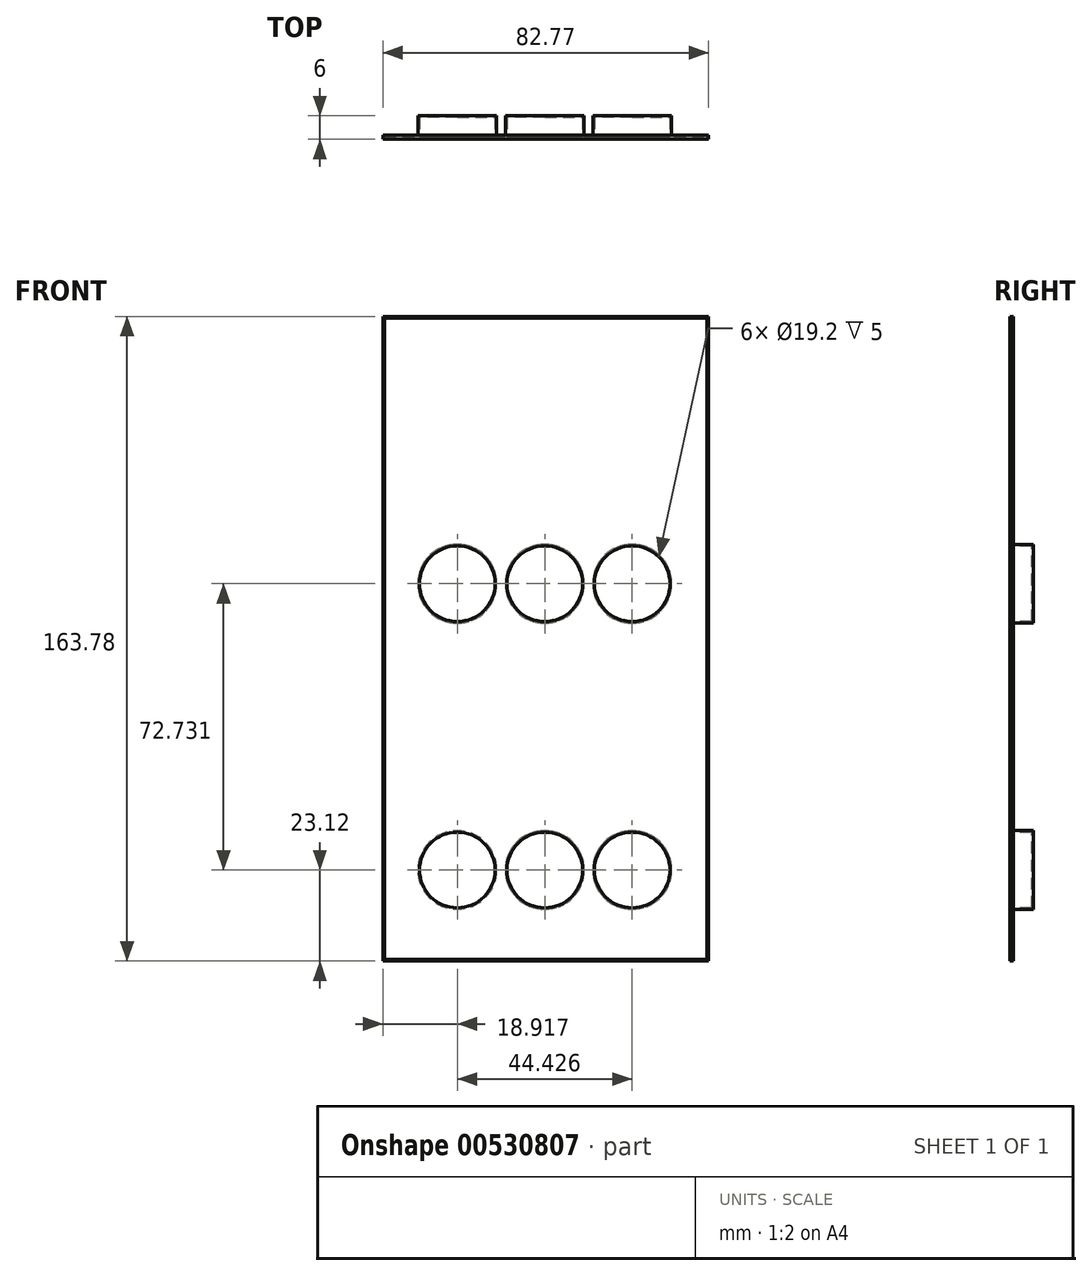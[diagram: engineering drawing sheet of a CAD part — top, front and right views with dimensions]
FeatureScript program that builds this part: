
annotation { "Feature Type Name" : "Feature", "Feature Type Description" : "" }
export const myFeature = defineFeature(function(context is Context, id is Id, definition is map)
    precondition{}
    {
        {
            var Q0;
            Q0=qCreatedBy(makeId("Front.planeOp"),FACE);
            var sketch = newSketch(context, id + "F0", { "sketchPlane" : qUnion([Q0])});
            skLineSegment(sketch, "E0.bottom", {"start": v(0, 0) * mm, "end": v(82.77, 0) * mm});
            skLineSegment(sketch, "E0.top", {"start": v(0, 163.78) * mm, "end": v(82.77, 163.78) * mm});
            skLineSegment(sketch, "E0.left", {"start": v(0, 0) * mm, "end": v(0, 163.78) * mm});
            skLineSegment(sketch, "E0.right", {"start": v(82.77, 0) * mm, "end": v(82.77, 163.78) * mm});
            skSolve(sketch);
        }
        {
            var Q0;
            Q0=makeQuery(id+"F0.imprint","IMPRINT",FACE,{"disambiguationData":[TD([[makeQuery(id+"F0.imprint","IMPRINT",EDGE,{"derivedFrom":sQuery(id+"F0.wireOp",EDGE,"E0.bottom")}),1.0]])]});
            extrude(context, id + "F1", {"entities" : qUnion([Q0]), "depth" : 1 * mm, "offsetDistance" : 25.4 * mm});
        }
        {
            var Q0;
            Q0=makeQuery(id+"F1.opExtrude","CAP_FACE",FACE,{"disambiguationData":[OSD([sQuery(id+"F0.wireOp",EDGE,"E0.bottom"),sQuery(id+"F0.wireOp",EDGE,"E0.top"),sQuery(id+"F0.wireOp",EDGE,"E0.left"),sQuery(id+"F0.wireOp",EDGE,"E0.right")])],"isStart":true});
            var sketch = newSketch(context, id + "F2", { "sketchPlane" : qUnion([Q0])});
            skCircle(sketch, "E1", {"center": v(-18.92, 23.12) * mm, "radius": 10 * mm});
            skCircle(sketch, "E2.0.1.0", {"center": v(-18.92, 95.85) * mm, "radius": 10 * mm});
            skCircle(sketch, "E2.1.0.0", {"center": v(-41.13, 23.12) * mm, "radius": 10 * mm});
            skCircle(sketch, "E2.1.1.0", {"center": v(-41.13, 95.85) * mm, "radius": 10 * mm});
            skCircle(sketch, "E2.2.0.0", {"center": v(-63.34, 23.12) * mm, "radius": 10 * mm});
            skCircle(sketch, "E2.2.1.0", {"center": v(-63.34, 95.85) * mm, "radius": 10 * mm});
            skLineSegment(sketch, "E2.direction1", {"start": v(-18.92, 23.12) * mm, "end": v(-41.13, 23.12) * mm, "construction": true});
            skLineSegment(sketch, "E2.direction2", {"start": v(-18.92, 23.12) * mm, "end": v(-18.92, 95.85) * mm, "construction": true});
            skSolve(sketch);
        }
        {
            var Q0;
            Q0 = qSketchRegion(id + "F2", true);
            extrude(context, id + "F3", {"entities" : qUnion([Q0]), "operationType" : NewBodyOperationType.ADD, "depth" : 5 * mm, "offsetDistance" : 25 * mm});
        }
        {
            var Q0;
            Q0=makeQuery(id+"F1.opExtrude","CAP_FACE",FACE,{"disambiguationData":[OSD([sQuery(id+"F0.wireOp",EDGE,"E0.bottom"),sQuery(id+"F0.wireOp",EDGE,"E0.top"),sQuery(id+"F0.wireOp",EDGE,"E0.left"),sQuery(id+"F0.wireOp",EDGE,"E0.right")])],"isStart":false});
            shell(context, id + "F4", {"entities" : qUnion([Q0]), "thickness" : 0.4 * mm});
        }
    });
